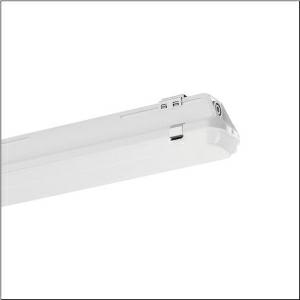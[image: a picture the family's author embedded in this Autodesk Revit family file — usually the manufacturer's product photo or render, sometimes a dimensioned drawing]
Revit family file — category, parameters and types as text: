
# Revit family: monsun_r__11_51fp20dp460l007_3abd
name_source: partatom
category: Lighting Fixtures
units: mm (PartAtom-declared; Revit-internal decimal feet)

## family parameters
Cut with Voids When Loaded = No
Host = Face
Light Source = No
Part Type = Normal
Room Calculation Point = No
Round Connector Dimension = Use Diameter
Shared = No

## types (1)
- --- (1 x LED, 5450 lm, 31.5 W, 4000K)
    Apparent Load = 32 VA
    CIE Flux Codes = 45 75 93 94 100
    Color Rendering = 80
    Color Temperature = 4000K
    Default Elevation = 1800 mm
    Description = Monsun® 11, damp-proof luminaire, chain hanger, primary optical cover: enclosure, of PC, light emission: direct distribution, primary light characteristic: symmetric, installation type: suspended mounting, surface-mounted, horizontal mounting, vertical mounting, LED, rated luminous flux: 5.450lm, luminous efficacy: 173lm/W, light colour: 840, colour temperature: 4000K, control gear: DALI 2, with terminal, 5-pole, max. 2.5mm², through-wiring: 7x 2.5mm², mains connection: 220..240V, AC, 50/60Hz, rated input power: 32W, housing, of glass-fibre reinforced polyester, uncoated, bright grey, incl. chain hanger, length: 1.590mm, width: 90mm, height: 88mm, clip for enclosure, of stainless steel (V2A), ceiling mounting element, of stainless steel (V2A), chain hanger, of stainless steel (V2A), protection rating (complete): IP66, insulation class (complete): insulation class I (protective earthing), certification: CE, ENEC, VDE, UKCA, protection symbol: D, impact resistance: IK08, permissible operating ambient temperature: -35..+40°C, standard: EN 50419, EN 60598-2-1, corresponds to IFS (International Featured Standards) requirements for safety and quality in the food industry, for indoor or canopied outdoor use, no direct snow, no direct sun, no direct rain, LABS conformity tested according to VDMA 24364:2018-05, contact your sales advisor before using the luminaires in applications with unclear chemical exposure, large temperature fluctuations or condensation-forming humidity, packaging unit: 1 piece
    Height = 89 mm
    Lamp = 1 x LED
    Lamp Light Flux = 5450 lm
    Lamp Power = 31.5 W
    Lamp count = 1
    Length = 1590 mm
    Luminous efficacy = 173 lm/W
    Manufacturer = Siteco
    ModVariant = No
    Model = 51FP20DP460L007
    Mounting Place = Ceiling
    Mounting Type = Surface mounted
    Number of Poles = 1
    OnlyDefault = Yes
    Power Factor = 1
    Product Name = Monsun® 11
    Product group = damp-proof luminaire
    ProductGroupID = 301
    Protection Class = Protection class I
    Protection Degree = IP 66
    RLX_Detail_Level = 1
    RLX_Emergency_Light_Flux = 0 lm
    RLX_Emergency_Type = 0
    RLX_Emergency_Type_DB = No
    RlxData = <blob elided: 92041 chars, md5=23688fbe>
    Socket = socket
    Standby Power = 0 W
    System Light Flux = 5450 lm
    System Power = 32 W
    Type Comments = factory setting: luminous flux: 100 % | dim-lin: 254 | 219 mA
    Type Image = l_1349237.jpg
    URL = http://relux.com
    VarID = @adj_038269
    Voltage = 0 V
    Weight = 0.00 kg
    Width = 90 mm

## geometry (parser evidence)
native form markers: Blend x4, Sweep x13
no freeform markers — native parametric forms only
